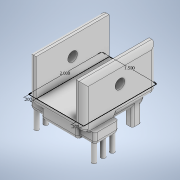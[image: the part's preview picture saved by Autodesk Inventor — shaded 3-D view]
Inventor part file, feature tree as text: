
AUTODESK INVENTOR PART (.ipt)
format: ipt  version: 2020 (Build 240168000, 168)  size: 553,984 bytes
history: native  units: in
note: dims shown in document units (in); Inventor stores cm internally (conversion verified against a paired STEP export)
features: sketch x5, extrude x4, fillet x3, hole x2
ambient origin geometry x8: Origin, YZ Plane, XZ Plane, XY Plane, X Axis, Y Axis, Z Axis, Center Point
bodies: Solid1 (feature_tree)
feature tree (14):
  sketch  "Sketch1"  dims[d0=1.5in d1=2.0in]
  extrude  "Extrusion1"  Depth=2.0in
  extrude  "Extrusion2"  Depth=0.2in
  hole  "Hole1"  [1 undecoded]
  extrude  "Extrusion3"  Depth=0.0625in
  extrude  "Extrusion4"  Depth=0.0625in
  hole  "Hole2"  [1 undecoded]
  fillet  "Fillet1"  Radius=0.25in
  fillet  "Fillet2"  Radius=0.25in
  fillet  "Fillet3"  [1 undecoded]
  sketch  "Sketch2"  dims[d2=0.2in d3=0.2in]
  sketch  "Sketch3"  dims[d4=1.0in d5=0.0in d6=0.2in d7=0.0in]
  sketch  "Sketch4"  dims[d8=0.5in]
  sketch  "Sketch5"  dims[d9=0.266in d10=0.75in d11=0.438in d12=0.25in d13=0.5635in d14=1.0in d15=0.8108in d16=1.0in d17=1.8425in d18=0.25in d19=0.25in d20=0.25in d21=180.0deg d22=0.7874in d23=0.0in d24=0.7874in d25=0.7874in d26=0.7874in d27=0.7874in d29=1.7717in d30=0.65in d31=0.3335in d32=0.0in d33=0.25in d34=0.25in d35=0.25in d36=0.7874in d37=0.7874in d38=0.1181in d39=0.1181in d40=0.1181in d41=0.1181in d42=0.1181in d43=0.1181in d44=0.4331in d45=0.0in d46=0.6693in d47=0.25in d48=0.089in d49=0.146in d50=0.75in d51=0.188in d52=0.5635in d53=0.224in d54=0.0in d55=0.125in d56=0.125in d57=0.0625in]
note: 3 required parameter values undecoded (feature->parameter linkage not recoverable at this tier; creation-order binding heuristic only, values carry confidence <= 0.55)
